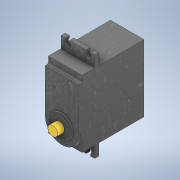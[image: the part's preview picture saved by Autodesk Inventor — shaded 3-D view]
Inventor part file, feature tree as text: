
AUTODESK INVENTOR PART (.ipt)
format: ipt  version: 2021 (Build 250183000, 183)  size: 226,816 bytes
history: native  units: mm
features: extrude x7, sketch x7, fillet x2, plane x1
ambient origin geometry x8: Origin, YZ Plane, XZ Plane, XY Plane, X Axis, Y Axis, Z Axis, Center Point
bodies: Solid1 (feature_tree)
feature tree (17):
  extrude  "Extrusion1"  Depth=40.0mm
  plane  "Work Plane1"
  extrude  "Extrusion2"  [1 undecoded]
  extrude  "Extrusion3"  Depth=3.9mm
  fillet  "Fillet1"  Radius=3.9mm
  fillet  "Fillet2"  Radius=3.8mm
  extrude  "Extrusion4"  Depth=2.5mm
  extrude  "Extrusion5"  Depth=2.0mm TaperAngle=0.0deg
  extrude  "Extrusion6"  Depth=1.0mm
  extrude  "Extrusion7"  Depth=1.0mm TaperAngle=0.0deg
  sketch  "Sketch1"  dims[d0=20.0mm d1=40.0mm]
  sketch  "Sketch2"  dims[d2=36.0mm d3=0.0mm d4=-10.0mm]
  sketch  "Sketch5"  dims[d5=6.8mm d6=3.9mm d7=3.9mm d8=3.8mm]
  sketch  "Sketch6"  dims[d9=3.8mm d10=2.5mm d11=2.5mm]
  sketch  "Sketch7"  dims[d12=2.5mm d13=0.0mm d14=2.0mm d15=0.0mm]
  sketch  "Sketch8"  dims[d16=1.0mm d17=1.0mm]
  sketch  "Sketch9"  dims[d18=13.5mm d19=1.0mm d20=0.0mm d21=11.0mm d22=0.5mm d23=0.0mm d24=5.8mm d25=4.0mm d26=0.0mm d27=1.0mm d28=0.0mm]
note: 1 required parameter value undecoded (feature->parameter linkage not recoverable at this tier; creation-order binding heuristic only, values carry confidence <= 0.55)
